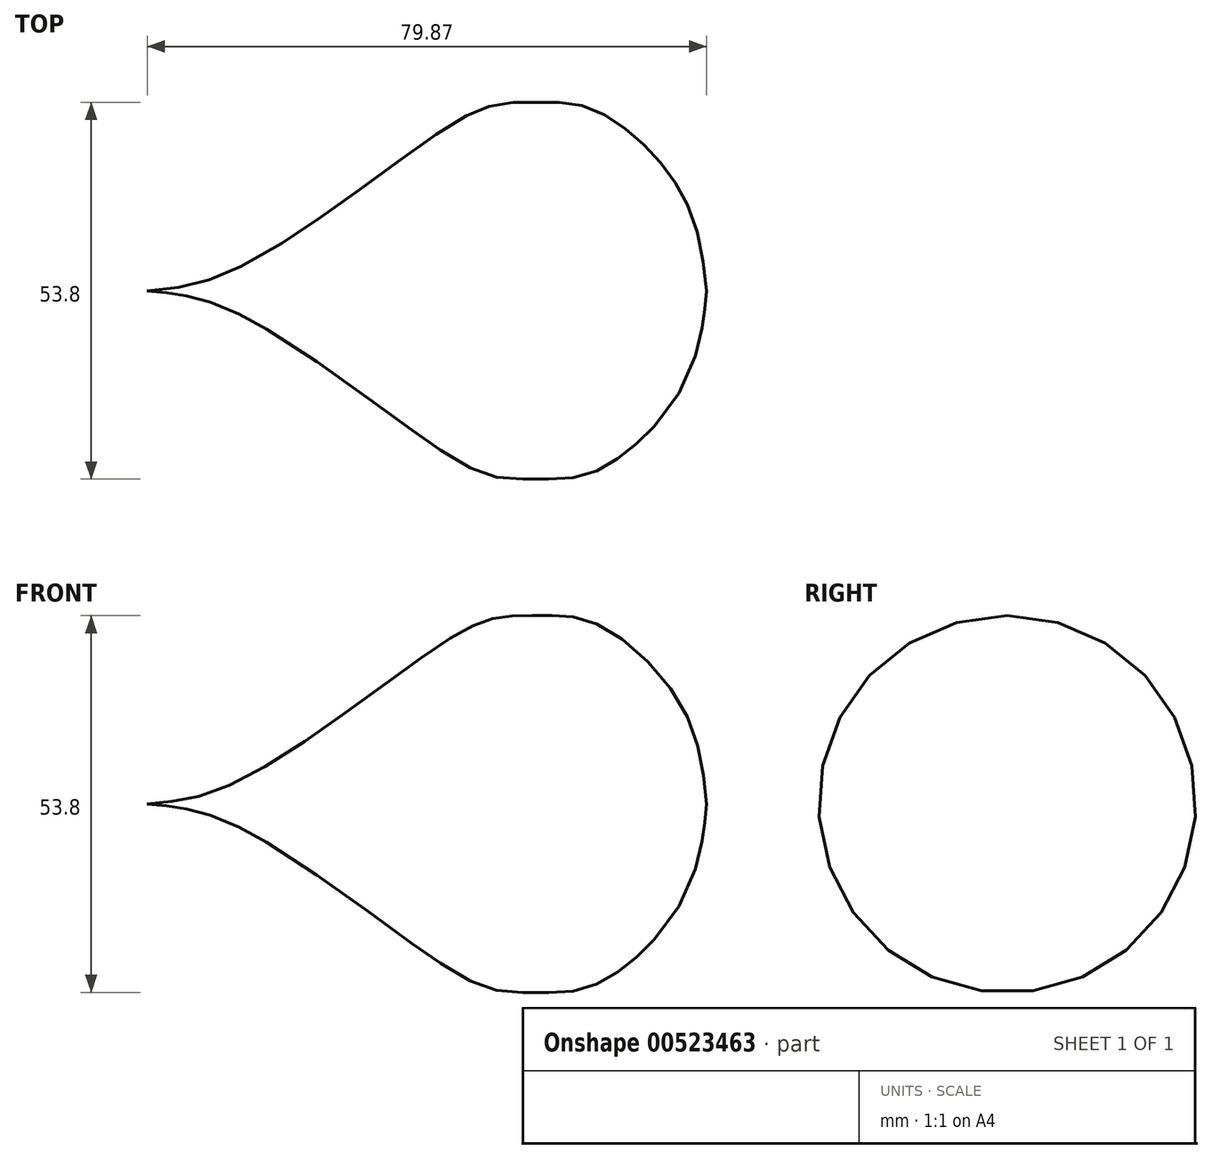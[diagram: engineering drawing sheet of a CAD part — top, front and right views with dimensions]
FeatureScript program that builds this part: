
annotation { "Feature Type Name" : "Feature", "Feature Type Description" : "" }
export const myFeature = defineFeature(function(context is Context, id is Id, definition is map)
    precondition{}
    {
        {
            var Q0;
            Q0=qCreatedBy(makeId("Front.planeOp"),FACE);
            var sketch = newSketch(context, id + "F0", { "sketchPlane" : qUnion([Q0])});
            skLineSegment(sketch, "E0.bottom", {"start": v(-0.26, 0.13) * mm, "end": v(79.61, 0.13) * mm});
            skLineSegment(sketch, "E0.top", {"start": v(-0.26, 32.56) * mm, "end": v(79.61, 32.56) * mm});
            skLineSegment(sketch, "E0.left", {"start": v(-0.26, 0.13) * mm, "end": v(-0.26, 32.56) * mm});
            skLineSegment(sketch, "E0.right", {"start": v(79.61, 0.13) * mm, "end": v(79.61, 32.56) * mm});
            skFitSpline(sketch, "E1", {"points": [v(-0.26, 0.13) * mm, v(12.52, 3.3) * mm, v(40.72, 22.28) * mm, v(49.69, 26.76) * mm, v(56.01, 27.02) * mm, v(63.66, 25.97) * mm, v(76.05, 14.1) * mm, v(79.61, 0.13) * mm], "startDerivative": vector(80.17, 6.58) * mm, "endDerivative": vector(10.05, -95.5) * mm});
            skSolve(sketch);
        }
        {
            var Q0;
            Q0=makeQuery(id+"F0.imprint","IMPRINT",FACE,{"disambiguationData":[TD([[makeQuery(id+"F0.imprint","IMPRINT",EDGE,{"derivedFrom":sQuery(id+"F0.wireOp",EDGE,"E0.bottom")}),1.0]])]});
            var Q1;
            Q1=sQuery(id+"F0.wireOp",EDGE,"E0.bottom");
            revolve(context, id + "F1", {"entities" : qUnion([Q0]), "axis" : qUnion([Q1]), "revolveType" : RevolveType.FULL});
        }
    });
